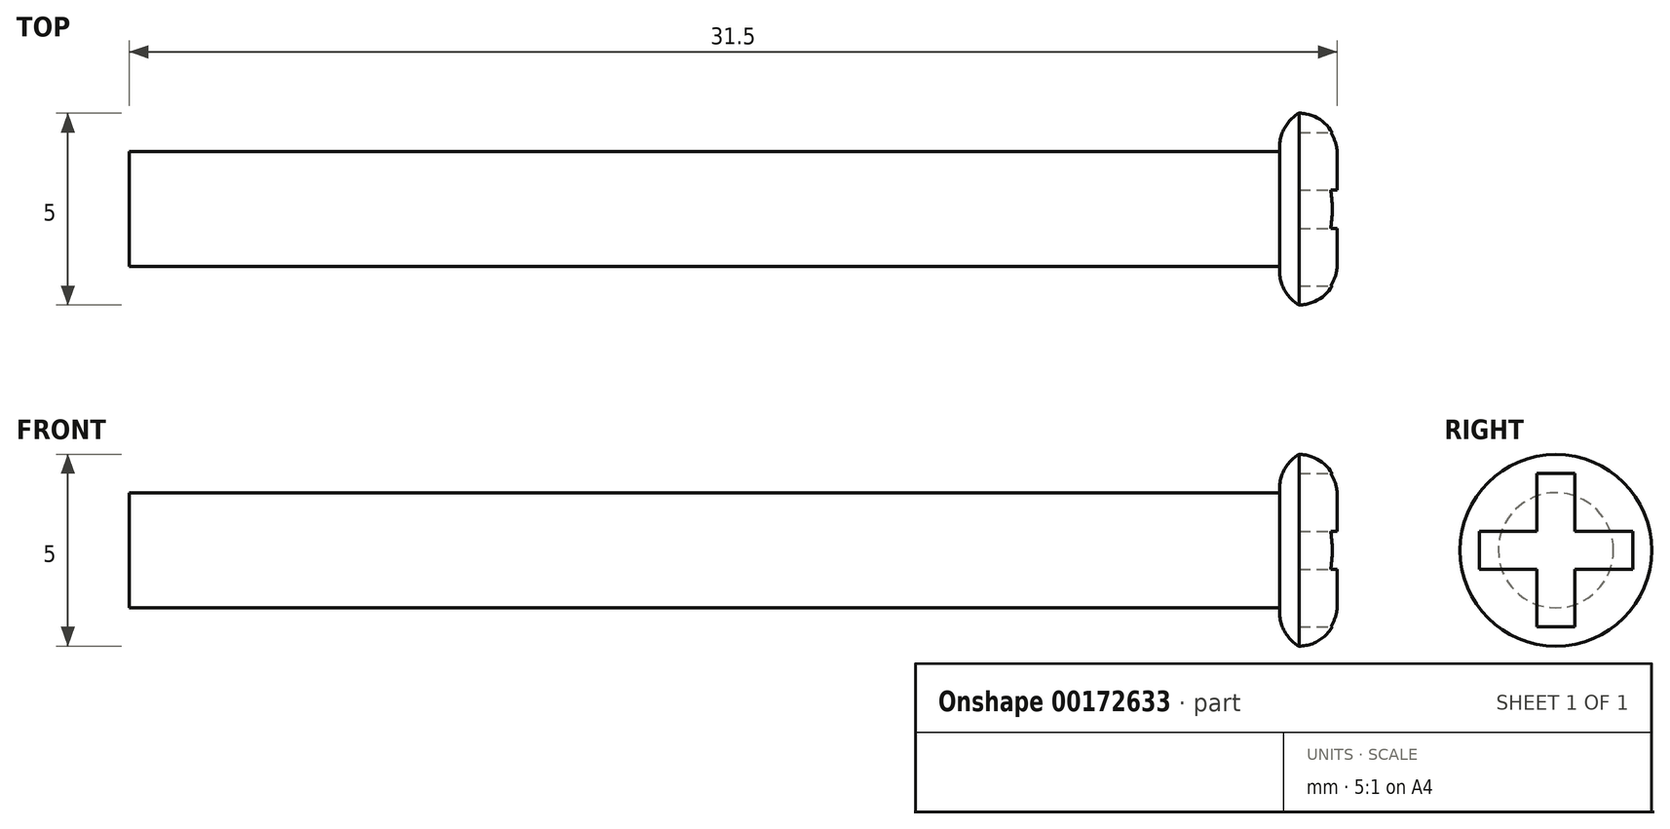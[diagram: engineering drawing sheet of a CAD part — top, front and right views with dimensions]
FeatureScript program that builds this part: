
annotation { "Feature Type Name" : "Feature", "Feature Type Description" : "" }
export const myFeature = defineFeature(function(context is Context, id is Id, definition is map)
    precondition{}
    {
        {
            var Q0;
            Q0=qCreatedBy(makeId("Top.planeOp"),FACE);
            var sketch = newSketch(context, id + "F0", { "sketchPlane" : qUnion([Q0])});
            skCircle(sketch, "E0", {"center": v(0, 0) * mm, "radius": 1.5 * mm});
            skSolve(sketch);
        }
        {
            var Q0;
            Q0=qSketchRegion(id+"F0",true);
            extrude(context, id + "F1", {"entities" : qUnion([Q0]), "depth" : 30 * mm});
        }
        {
            var Q0;
            Q0=makeQuery(id+"F1.opExtrude","CAP_FACE",FACE,{"disambiguationData":[OSD([sQuery(id+"F0.wireOp",EDGE,"E0")])],"isStart":false});
            var sketch = newSketch(context, id + "F2", { "sketchPlane" : qUnion([Q0])});
            skCircle(sketch, "E1", {"center": v(0, 0) * mm, "radius": 2.5 * mm});
            skSolve(sketch);
        }
        {
            var Q0;
            Q0=qSketchRegion(id+"F2",true);
            extrude(context, id + "F3", {"entities" : qUnion([Q0]), "operationType" : NewBodyOperationType.ADD, "depth" : 1.5 * mm});
        }
        {
            var Q0;
            Q0=makeQuery(id+"F3.opExtrude","CAP_FACE",FACE,{"disambiguationData":[OSD([sQuery(id+"F2.wireOp",EDGE,"E1")])],"isStart":false});
            var sketch = newSketch(context, id + "F4", { "sketchPlane" : qUnion([Q0])});
            skLineSegment(sketch, "E2.bottom", {"start": v(-0.5, 2) * mm, "end": v(0.5, 2) * mm});
            skLineSegment(sketch, "E2.top", {"start": v(-0.5, -2) * mm, "end": v(0.5, -2) * mm});
            skLineSegment(sketch, "E2.left", {"start": v(-0.5, 2) * mm, "end": v(-0.5, -2) * mm});
            skLineSegment(sketch, "E2.right", {"start": v(0.5, 2) * mm, "end": v(0.5, -2) * mm});
            skPoint(sketch, "E2.middle", {"position": v(0, 0) * mm});
            skLineSegment(sketch, "E3.bottom", {"start": v(-2, 0.5) * mm, "end": v(2, 0.5) * mm});
            skLineSegment(sketch, "E3.top", {"start": v(-2, -0.5) * mm, "end": v(2, -0.5) * mm});
            skLineSegment(sketch, "E3.left", {"start": v(-2, 0.5) * mm, "end": v(-2, -0.5) * mm});
            skLineSegment(sketch, "E3.right", {"start": v(2, 0.5) * mm, "end": v(2, -0.5) * mm});
            skSolve(sketch);
        }
        {
            var Q0;
            Q0=qSketchRegion(id+"F4",true);
            extrude(context, id + "F5", {"entities" : qUnion([Q0]), "operationType" : NewBodyOperationType.REMOVE, "oppositeDirection" : true, "depth" : 1 * mm});
        }
        {
            var Q0;
            Q0=makeQuery(id+"F3.opExtrude","CAP_EDGE",EDGE,{"disambiguationData":[OSD([sQuery(id+"F2.wireOp",EDGE,"E1")])],"isStart":false});
            fillet(context, id + "F6", {"entities" : qUnion([Q0]), "radius" : 1 * mm, "tangentPropagation" : true, "allowEdgeOverflow" : false});
        }
        {
            var Q0;
            Q0=makeQuery(id+"F3.opExtrude","CAP_EDGE",EDGE,{"disambiguationData":[OSD([sQuery(id+"F2.wireOp",EDGE,"E1")])],"isStart":true});
            fillet(context, id + "F7", {"entities" : qUnion([Q0]), "radius" : 1 * mm, "tangentPropagation" : true, "allowEdgeOverflow" : false});
        }
        {
            var Q0;
            Q0=qCreatedBy(makeId("Top.planeOp"),FACE);
            var sketch = newSketch(context, id + "F8", { "sketchPlane" : qUnion([Q0])});
            skLineSegment(sketch, "E4", {"start": v(0, -11.08) * mm, "end": v(0, 13.57) * mm, "construction": true});
            skSolve(sketch);
        }
        {
            var Q0;
            Q0=makeQuery(id+"F1.opExtrude","SWEPT_BODY",BODY,{"disambiguationData":[OSD([sQuery(id+"F0.wireOp",EDGE,"E0")])]});
            var Q1;
            Q1=sQuery(id+"F8.wireOp",EDGE,"E4");
            transform(context, id + "F9", {"entities" : qUnion([Q0]), "transformType" : TransformType.ROTATION, "transformAxis" : qUnion([Q1]), "angle" : 90 * degree, "makeCopy" : false});
        }
    });
